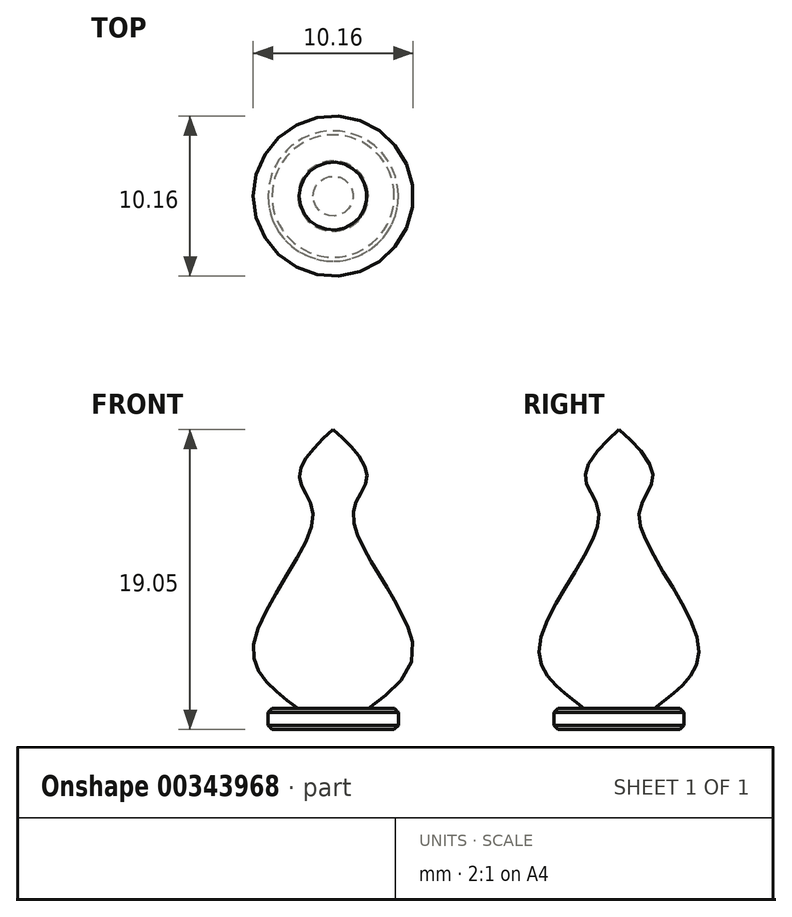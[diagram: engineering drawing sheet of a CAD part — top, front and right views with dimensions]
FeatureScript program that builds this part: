
annotation { "Feature Type Name" : "Feature", "Feature Type Description" : "" }
export const myFeature = defineFeature(function(context is Context, id is Id, definition is map)
    precondition{}
    {
        {
            var Q0;
            Q0=qCreatedBy(makeId("Front.planeOp"),FACE);
            var sketch = newSketch(context, id + "F0", { "sketchPlane" : qUnion([Q0])});
            skFitSpline(sketch, "E0", {"points": [v(-2.24, 1.35) * mm, v(-5.08, 5.1) * mm, v(-1.27, 13.38) * mm, v(-2.15, 16.02) * mm, v(0, 19.05) * mm], "startDerivative": vector(-14.93, 11.4) * mm, "endDerivative": vector(14.63, 12.89) * mm});
            skLineSegment(sketch, "E1", {"start": v(-2.24, 1.35) * mm, "end": v(-4.14, 1.35) * mm});
            skLineSegment(sketch, "E2", {"start": v(-4.14, 1.35) * mm, "end": v(-4.14, 0) * mm});
            skLineSegment(sketch, "E3", {"start": v(-4.14, 0) * mm, "end": v(0, 0) * mm});
            skLineSegment(sketch, "E4", {"start": v(0, 19.05) * mm, "end": v(0, 0) * mm});
            skSolve(sketch);
        }
        {
            var Q0;
            Q0 = qSketchRegion(id + "F0", true);
            var Q1;
            Q1=sQuery(id+"F0.wireOp",EDGE,"E4");
            revolve(context, id + "F1", {"entities" : qUnion([Q0]), "axis" : qUnion([Q1]), "revolveType" : RevolveType.FULL});
        }
        {
            var Q0;
            Q0=makeQuery(id+"F1.opRevolve","SWEPT_EDGE",EDGE,{"disambiguationData":[OSD([sQuery(id+"F0.wireOp",EDGE,"E1"),sQuery(id+"F0.wireOp",EDGE,"E2")])]});
            var Q1;
            Q1=makeQuery(id+"F1.opRevolve","SWEPT_FACE",FACE,{"disambiguationData":[OSD([sQuery(id+"F0.wireOp",EDGE,"E2")])]});
            chamfer(context, id + "F2", {"entities" : qUnion([Q0, Q1]), "width" : 0.25 * mm, "tangentPropagation" : true});
        }
    });
